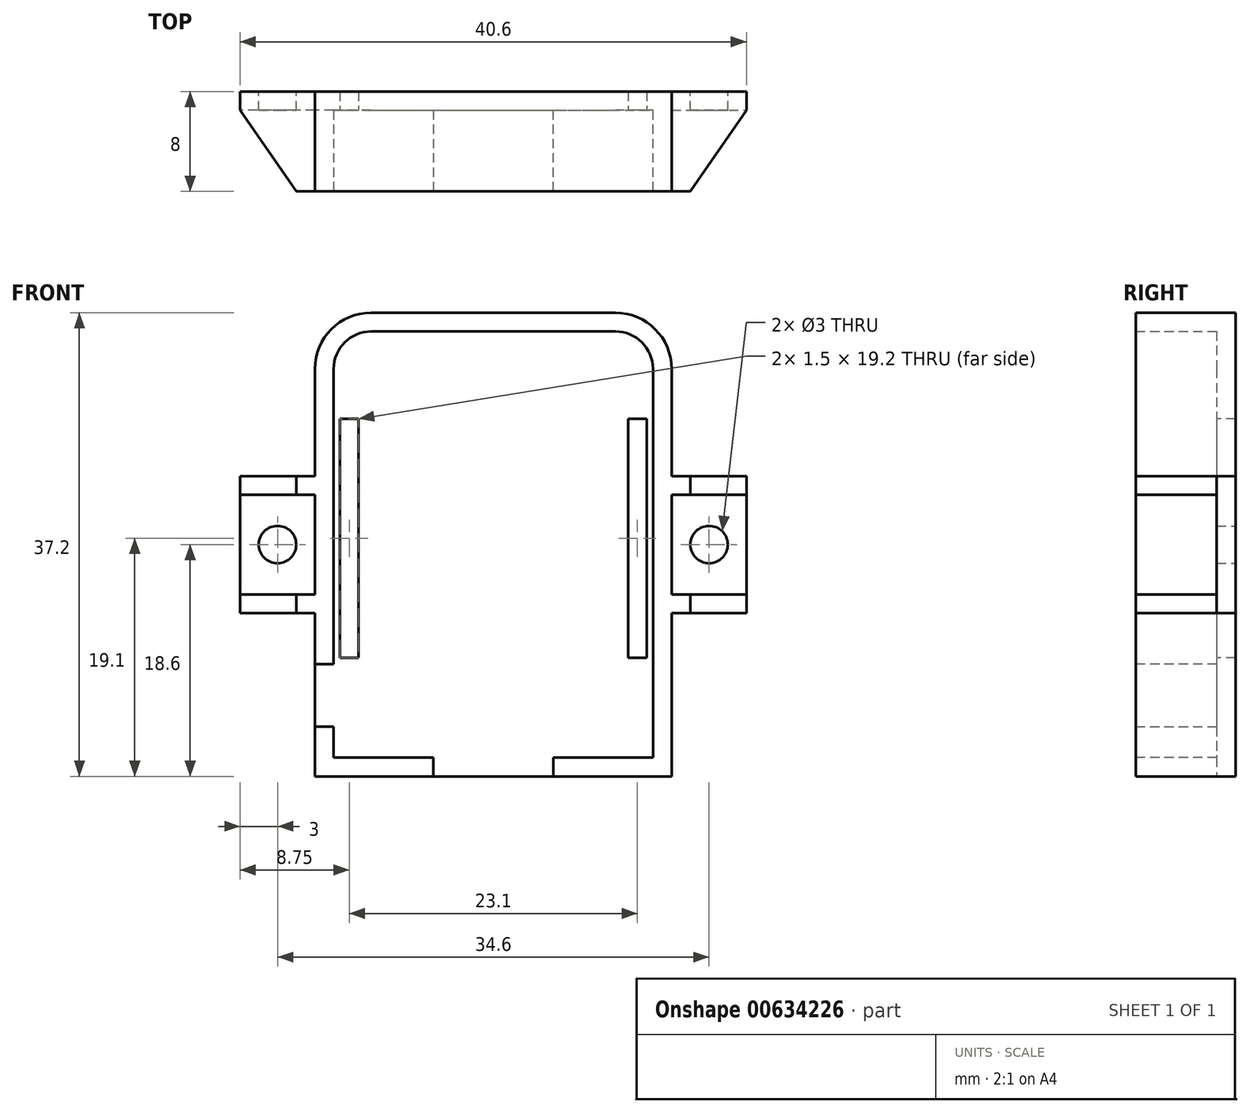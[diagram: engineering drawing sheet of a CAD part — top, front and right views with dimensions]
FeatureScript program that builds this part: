
annotation { "Feature Type Name" : "Feature", "Feature Type Description" : "" }
export const myFeature = defineFeature(function(context is Context, id is Id, definition is map)
    precondition{}
    {
        {
            var Q0;
            Q0=qCreatedBy(makeId("Front.planeOp"),FACE);
            var sketch = newSketch(context, id + "F0", { "sketchPlane" : qUnion([Q0])});
            skLineSegment(sketch, "E0.bottom", {"start": v(-22.6, 34.2) * mm, "end": v(-3, 34.2) * mm});
            skLineSegment(sketch, "E0.top", {"start": v(-25.6, 0) * mm, "end": v(0, 0) * mm});
            skLineSegment(sketch, "E0.left", {"start": v(-25.6, 31.2) * mm, "end": v(-25.6, 0) * mm});
            skLineSegment(sketch, "E0.right", {"start": v(0, 31.2) * mm, "end": v(0, 0) * mm});
            skPoint(sketch, "E1.visualSharp", {"position": v(-25.6, 34.2) * mm});
            skArc(sketch, "E1.filletArc", {"start": v(-22.6, 34.2) * mm, "mid": v(-24.72, 33.32) * mm, "end": v(-25.6, 31.2) * mm});
            skPoint(sketch, "E2.visualSharp", {"position": v(0, 34.2) * mm});
            skArc(sketch, "E2.filletArc", {"start": v(0, 31.2) * mm, "mid": v(-0.88, 33.32) * mm, "end": v(-3, 34.2) * mm});
            skLineSegment(sketch, "E3", {"start": v(-27.1, -1.5) * mm, "end": v(1.5, -1.5) * mm});
            skLineSegment(sketch, "E4", {"start": v(1.5, -1.5) * mm, "end": v(1.5, 31.2) * mm});
            skLineSegment(sketch, "E5", {"start": v(-3, 35.7) * mm, "end": v(-22.6, 35.7) * mm});
            skLineSegment(sketch, "E6", {"start": v(-27.1, -1.5) * mm, "end": v(-27.1, 31.2) * mm});
            skPoint(sketch, "E7.visualSharp", {"position": v(1.5, 35.7) * mm});
            skArc(sketch, "E7.filletArc", {"start": v(1.5, 31.2) * mm, "mid": v(0.18, 34.38) * mm, "end": v(-3, 35.7) * mm});
            skPoint(sketch, "E8.visualSharp", {"position": v(-27.1, 35.7) * mm});
            skArc(sketch, "E8.filletArc", {"start": v(-22.6, 35.7) * mm, "mid": v(-25.78, 34.38) * mm, "end": v(-27.1, 31.2) * mm});
            skLineSegment(sketch, "E9", {"start": v(-12.8, -17.14) * mm, "end": v(-12.8, 40.07) * mm, "construction": true});
            skLineSegment(sketch, "E10.bottom", {"start": v(1.5, 21.1) * mm, "end": v(7.5, 21.1) * mm});
            skLineSegment(sketch, "E10.top", {"start": v(1.5, 13.1) * mm, "end": v(7.5, 13.1) * mm});
            skLineSegment(sketch, "E10.left", {"start": v(1.5, 21.1) * mm, "end": v(1.5, 13.1) * mm});
            skLineSegment(sketch, "E10.right", {"start": v(7.5, 21.1) * mm, "end": v(7.5, 13.1) * mm});
            skLineSegment(sketch, "E11", {"start": v(-37, 17.1) * mm, "end": v(14.36, 17.1) * mm, "construction": true});
            skCircle(sketch, "E12", {"center": v(4.5, 17.1) * mm, "radius": 1.5 * mm});
            skLineSegment(sketch, "E13", {"start": v(7.5, 21.1) * mm, "end": v(7.5, 22.6) * mm});
            skLineSegment(sketch, "E14", {"start": v(7.5, 22.6) * mm, "end": v(1.5, 22.6) * mm});
            skLineSegment(sketch, "E15", {"start": v(7.5, 13.1) * mm, "end": v(7.5, 11.6) * mm});
            skLineSegment(sketch, "E16", {"start": v(7.5, 11.6) * mm, "end": v(1.5, 11.6) * mm});
            skLineSegment(sketch, "E17.MirrorCS", {"start": v(-33.1, 22.6) * mm, "end": v(-27.1, 22.6) * mm});
            skLineSegment(sketch, "E18.MirrorCS", {"start": v(-27.1, 21.1) * mm, "end": v(-33.1, 21.1) * mm});
            skCircle(sketch, "E19.MirrorC", {"center": v(-30.1, 17.1) * mm, "radius": 1.5 * mm});
            skLineSegment(sketch, "E20.MirrorCS", {"start": v(-27.1, 13.1) * mm, "end": v(-33.1, 13.1) * mm});
            skLineSegment(sketch, "E21.MirrorCS", {"start": v(-33.1, 11.6) * mm, "end": v(-27.1, 11.6) * mm});
            skLineSegment(sketch, "E22.MirrorCS", {"start": v(-33.1, 21.1) * mm, "end": v(-33.1, 13.1) * mm});
            skLineSegment(sketch, "E23.MirrorCS", {"start": v(-33.1, 21.1) * mm, "end": v(-33.1, 22.6) * mm});
            skLineSegment(sketch, "E24.MirrorCS", {"start": v(-33.1, 13.1) * mm, "end": v(-33.1, 11.6) * mm});
            skSolve(sketch);
        }
        {
            var Q0;
            {var subQ0=sQuery(id+"F0.wireOp",EDGE,"E10.top");Q0=makeQuery(id+"F0.imprint","IMPRINT",FACE,{"disambiguationData":[TD([[makeQuery(id+"F0.imprint","IMPRINT",EDGE,{"derivedFrom":subQ0}),-1.0]])]});}
            var Q1;
            {var subQ0=sQuery(id+"F0.wireOp",EDGE,"E10.bottom");Q1=makeQuery(id+"F0.imprint","IMPRINT",FACE,{"disambiguationData":[TD([[makeQuery(id+"F0.imprint","IMPRINT",EDGE,{"derivedFrom":subQ0}),1.0]])]});}
            var Q2;
            {var subQ0=sQuery(id+"F0.wireOp",EDGE,"E20.MirrorCS");Q2=makeQuery(id+"F0.imprint","IMPRINT",FACE,{"disambiguationData":[TD([[makeQuery(id+"F0.imprint","IMPRINT",EDGE,{"derivedFrom":subQ0}),1.0]])]});}
            var Q3;
            {var subQ0=sQuery(id+"F0.wireOp",EDGE,"E17.MirrorCS");Q3=makeQuery(id+"F0.imprint","IMPRINT",FACE,{"disambiguationData":[TD([[makeQuery(id+"F0.imprint","IMPRINT",EDGE,{"derivedFrom":subQ0}),-1.0]])]});}
            var Q4;
            Q4=makeQuery(id+"F0.imprint","IMPRINT",FACE,{"disambiguationData":[TD([[makeQuery(id+"F0.imprint","IMPRINT",EDGE,{"derivedFrom":sQuery(id+"F0.wireOp",EDGE,"E0.bottom")}),1.0]])]});
            extrude(context, id + "F1", {"entities" : qUnion([Q0, Q1, Q2, Q3, Q4]), "depth" : 8 * mm, "offsetDistance" : 25 * mm});
        }
        {
            var Q0;
            Q0=makeQuery(id+"F0.imprint","IMPRINT",FACE,{"disambiguationData":[TD([[makeQuery(id+"F0.imprint","IMPRINT",EDGE,{"derivedFrom":sQuery(id+"F0.wireOp",EDGE,"E10.bottom")}),-1.0]])]});
            var Q1;
            {var subQ1=sQuery(id+"F0.wireOp",EDGE,"E18.MirrorCS");Q1=makeQuery(id+"F0.imprint","IMPRINT",FACE,{"disambiguationData":[TD([[makeQuery(id+"F0.imprint","IMPRINT",EDGE,{"derivedFrom":subQ1}),1.0]])]});}
            var Q2;
            Q2=makeQuery(id+"F0.imprint","IMPRINT",FACE,{"disambiguationData":[TD([[makeQuery(id+"F0.imprint","IMPRINT",EDGE,{"derivedFrom":sQuery(id+"F0.wireOp",EDGE,"E0.bottom")}),-1.0]])]});
            extrude(context, id + "F2", {"entities" : qUnion([Q0, Q1, Q2]), "operationType" : NewBodyOperationType.ADD, "depth" : 1.5 * mm, "offsetDistance" : 25 * mm});
        }
        {
            var Q0;
            Q0=makeQuery(id+"F1.opExtrude","SWEPT_FACE",FACE,{"disambiguationData":[OSD([sQuery(id+"F0.wireOp",EDGE,"E16")])]});
            var sketch = newSketch(context, id + "F3", { "sketchPlane" : qUnion([Q0])});
            skLineSegment(sketch, "E25", {"start": v(3, 8) * mm, "end": v(7.5, 1.5) * mm});
            skLineSegment(sketch, "E26", {"start": v(7.5, 1.5) * mm, "end": v(7.5, 8) * mm});
            skLineSegment(sketch, "E27", {"start": v(7.5, 8) * mm, "end": v(3, 8) * mm});
            skSolve(sketch);
        }
        {
            var Q0;
            Q0=makeQuery(id+"F3.imprint","IMPRINT",FACE,{"disambiguationData":[TD([[makeQuery(id+"F3.imprint","IMPRINT",EDGE,{"derivedFrom":sQuery(id+"F3.wireOp",EDGE,"E25")}),1.0]])]});
            extrude(context, id + "F4", {"entities" : qUnion([Q0]), "operationType" : NewBodyOperationType.REMOVE, "oppositeDirection" : true, "depth" : 25 * mm, "offsetDistance" : 25 * mm});
        }
        {
            var Q0;
            Q0=makeQuery(id+"F1.opExtrude","SWEPT_FACE",FACE,{"disambiguationData":[OSD([sQuery(id+"F0.wireOp",EDGE,"E21.MirrorCS")])]});
            var sketch = newSketch(context, id + "F5", { "sketchPlane" : qUnion([Q0])});
            skLineSegment(sketch, "E28", {"start": v(-28.6, 8) * mm, "end": v(-33.1, 1.5) * mm});
            skLineSegment(sketch, "E29", {"start": v(-33.1, 1.5) * mm, "end": v(-33.1, 8) * mm});
            skLineSegment(sketch, "E30", {"start": v(-33.1, 8) * mm, "end": v(-28.6, 8) * mm});
            skSolve(sketch);
        }
        {
            var Q0;
            Q0=makeQuery(id+"F5.imprint","IMPRINT",FACE,{"disambiguationData":[TD([[makeQuery(id+"F5.imprint","IMPRINT",EDGE,{"derivedFrom":sQuery(id+"F5.wireOp",EDGE,"E28")}),-1.0]])]});
            extrude(context, id + "F6", {"entities" : qUnion([Q0]), "operationType" : NewBodyOperationType.REMOVE, "oppositeDirection" : true, "depth" : 25 * mm, "offsetDistance" : 25 * mm});
        }
        {
            var Q0;
            Q0=makeQuery(id+"F1.opExtrude","SWEPT_FACE",FACE,{"disambiguationData":[OSD([sQuery(id+"F0.wireOp",EDGE,"E3")])]});
            var sketch = newSketch(context, id + "F7", { "sketchPlane" : qUnion([Q0])});
            skLineSegment(sketch, "E31", {"start": v(-17.6, 1.5) * mm, "end": v(-8, 1.5) * mm});
            skLineSegment(sketch, "E32", {"start": v(-17.6, 1.5) * mm, "end": v(-17.6, 8) * mm});
            skLineSegment(sketch, "E33", {"start": v(-17.6, 8) * mm, "end": v(-8, 8) * mm});
            skPoint(sketch, "E33.endSnap0", {"position": v(-12.8, 8) * mm});
            skLineSegment(sketch, "E34", {"start": v(-8, 8) * mm, "end": v(-8, 1.5) * mm});
            skSolve(sketch);
        }
        {
            var Q0;
            Q0=makeQuery(id+"F7.imprint","IMPRINT",FACE,{"disambiguationData":[TD([[makeQuery(id+"F7.imprint","IMPRINT",EDGE,{"derivedFrom":sQuery(id+"F7.wireOp",EDGE,"IJSsB6SE-eJ08-FWvL-wHjC-QON1tO38z0Xt")}),1.0]])]});
            var Q1;
            Q1=makeQuery(id+"F7.imprint","IMPRINT",FACE,{"disambiguationData":[TD([[makeQuery(id+"F7.imprint","IMPRINT",EDGE,{"derivedFrom":sQuery(id+"F7.wireOp",EDGE,"E31")}),1.0]])]});
            extrude(context, id + "F8", {"entities" : qUnion([Q0, Q1]), "operationType" : NewBodyOperationType.REMOVE, "endBound" : BoundingType.UP_TO_NEXT, "oppositeDirection" : true, "depth" : 2 * mm, "offsetDistance" : 25 * mm});
        }
        {
            var Q0;
            {var subQ0=sQuery(id+"F0.wireOp",EDGE,"E6");Q0=makeQuery(id+"F1.opExtrude","SWEPT_FACE",FACE,{"disambiguationData":[OSD([subQ0]),TDD([makeQuery(id+"F0.imprint","IMPRINT",EDGE,{"disambiguationData":[TD([[makeQuery(id+"F0.imprint","INTERSECT",VERTEX,{"derivedFrom":[sQuery(id+"F0.wireOp",EDGE,"E3"),subQ0]}),-1.0]])],"derivedFrom":subQ0})])]});}
            var sketch = newSketch(context, id + "F9", { "sketchPlane" : qUnion([Q0])});
            skLineSegment(sketch, "E35", {"start": v(1.5, 7.5) * mm, "end": v(1.5, 2.5) * mm});
            skLineSegment(sketch, "E36", {"start": v(1.5, 7.5) * mm, "end": v(8, 7.5) * mm});
            skLineSegment(sketch, "E37", {"start": v(8, 7.5) * mm, "end": v(8, 2.5) * mm});
            skLineSegment(sketch, "E38", {"start": v(8, 2.5) * mm, "end": v(1.5, 2.5) * mm});
            skSolve(sketch);
        }
        {
            var Q0;
            Q0=makeQuery(id+"F9.imprint","IMPRINT",FACE,{"disambiguationData":[TD([[makeQuery(id+"F9.imprint","IMPRINT",EDGE,{"derivedFrom":sQuery(id+"F9.wireOp",EDGE,"E35")}),1.0]])]});
            extrude(context, id + "F10", {"entities" : qUnion([Q0]), "operationType" : NewBodyOperationType.REMOVE, "endBound" : BoundingType.UP_TO_NEXT, "oppositeDirection" : true, "depth" : 25 * mm, "offsetDistance" : 25 * mm});
        }
        {
            var Q0;
            Q0=makeQuery(id+"F10.boolean.opBoolean","MERGE",FACE,{"derivedFrom":[makeQuery(id+"F8.boolean.opBoolean","MERGE",FACE,{"derivedFrom":[makeQuery(id+"F2.opExtrude","CAP_FACE",FACE,{"disambiguationData":[OSD([sQuery(id+"F0.wireOp",EDGE,"E0.bottom"),sQuery(id+"F0.wireOp",EDGE,"E0.top"),sQuery(id+"F0.wireOp",EDGE,"E0.left"),sQuery(id+"F0.wireOp",EDGE,"E0.right"),sQuery(id+"F0.wireOp",EDGE,"E1.filletArc"),sQuery(id+"F0.wireOp",EDGE,"E2.filletArc")])],"isStart":false}),makeQuery(id+"F8.opExtrude","SWEPT_FACE",FACE,{"disambiguationData":[OSD([sQuery(id+"F7.wireOp",EDGE,"E31")])]})]}),makeQuery(id+"F10.opExtrude","SWEPT_FACE",FACE,{"disambiguationData":[OSD([sQuery(id+"F9.wireOp",EDGE,"E35")])]})]});
            var sketch = newSketch(context, id + "F11", { "sketchPlane" : qUnion([Q0])});
            skLineSegment(sketch, "E39.bottom", {"start": v(-25.1, 27.2) * mm, "end": v(-23.6, 27.2) * mm});
            skLineSegment(sketch, "E39.top", {"start": v(-25.1, 8) * mm, "end": v(-23.6, 8) * mm});
            skLineSegment(sketch, "E39.left", {"start": v(-25.1, 27.2) * mm, "end": v(-25.1, 8) * mm});
            skLineSegment(sketch, "E39.right", {"start": v(-23.6, 27.2) * mm, "end": v(-23.6, 8) * mm});
            skLineSegment(sketch, "E40.MirrorCS", {"start": v(-2, 27.2) * mm, "end": v(-2, 8) * mm});
            skLineSegment(sketch, "E41.MirrorCS", {"start": v(-0.5, 27.2) * mm, "end": v(-0.5, 8) * mm});
            skLineSegment(sketch, "E42.MirrorCS", {"start": v(-0.5, 27.2) * mm, "end": v(-2, 27.2) * mm});
            skLineSegment(sketch, "E43.MirrorCS", {"start": v(-0.5, 8) * mm, "end": v(-2, 8) * mm});
            skSolve(sketch);
        }
        {
            var Q0;
            Q0=makeQuery(id+"F11.imprint","IMPRINT",FACE,{"disambiguationData":[TD([[makeQuery(id+"F11.imprint","IMPRINT",EDGE,{"derivedFrom":sQuery(id+"F11.wireOp",EDGE,"E39.bottom")}),-1.0]])]});
            var Q1;
            Q1=makeQuery(id+"F11.imprint","IMPRINT",FACE,{"disambiguationData":[TD([[makeQuery(id+"F11.imprint","IMPRINT",EDGE,{"derivedFrom":sQuery(id+"F11.wireOp",EDGE,"E40.MirrorCS")}),1.0]])]});
            extrude(context, id + "F12", {"entities" : qUnion([Q0, Q1]), "operationType" : NewBodyOperationType.REMOVE, "endBound" : BoundingType.UP_TO_NEXT, "oppositeDirection" : true, "depth" : 25 * mm, "offsetDistance" : 25 * mm});
        }
    });
